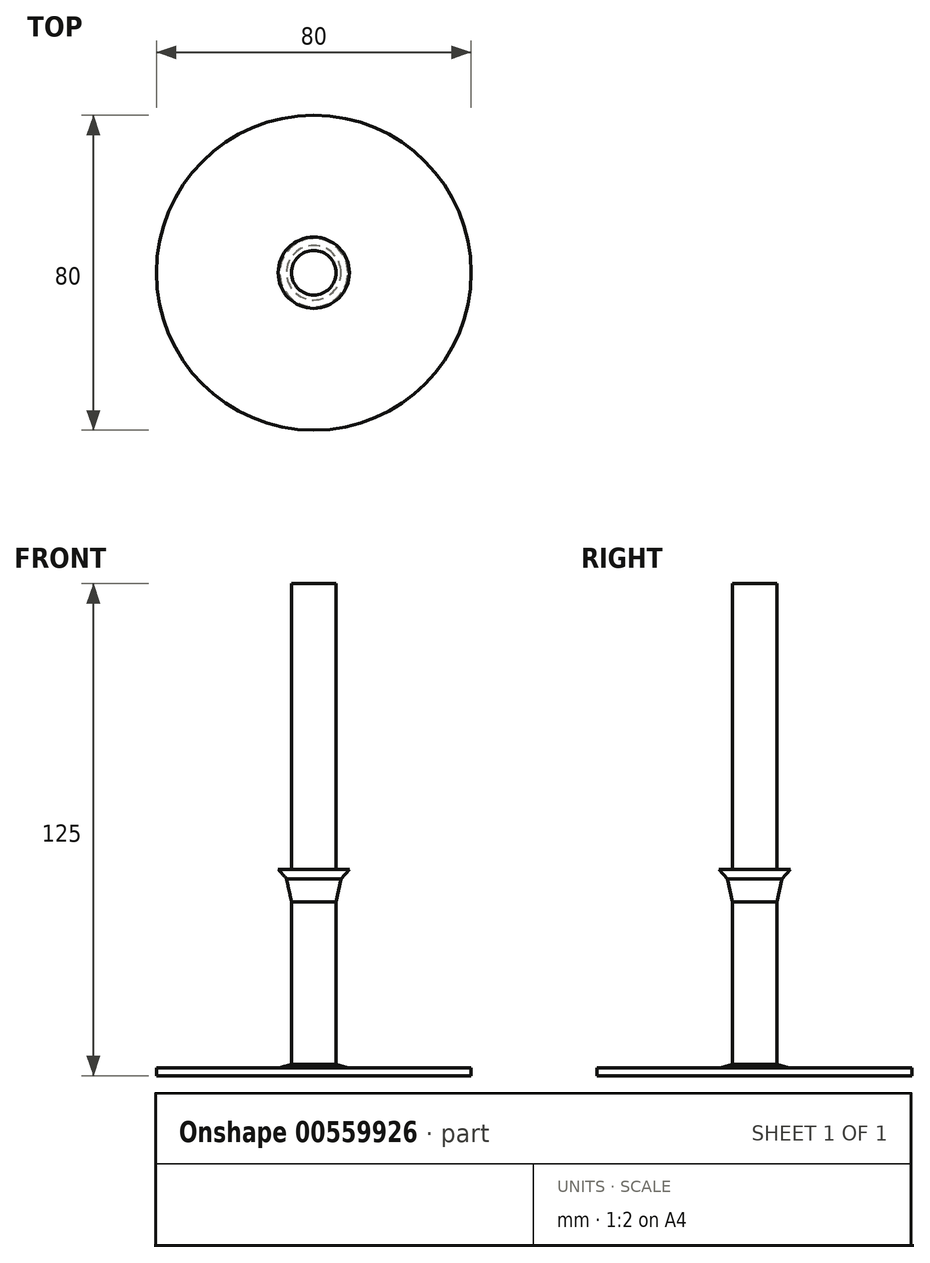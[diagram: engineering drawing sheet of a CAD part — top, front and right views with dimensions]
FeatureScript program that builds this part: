
annotation { "Feature Type Name" : "Feature", "Feature Type Description" : "" }
export const myFeature = defineFeature(function(context is Context, id is Id, definition is map)
    precondition{}
    {
        {
            var Q0;
            Q0=qCreatedBy(makeId("Front.planeOp"),FACE);
            var sketch = newSketch(context, id + "F0", { "sketchPlane" : qUnion([Q0])});
            skLineSegment(sketch, "E0", {"start": v(0, 0) * mm, "end": v(-40, 0) * mm});
            skLineSegment(sketch, "E1", {"start": v(-40, 0) * mm, "end": v(-40, 2) * mm});
            skLineSegment(sketch, "E2", {"start": v(-40, 2) * mm, "end": v(-19.77, 2) * mm});
            skLineSegment(sketch, "E3", {"start": v(-5.65, 58.65) * mm, "end": v(-5.65, 125) * mm});
            skPoint(sketch, "E4.start.orphan", {"position": v(-5.65, 63.5) * mm});
            skPoint(sketch, "E5.newPointB", {"position": v(0, 2) * mm});
            skLineSegment(sketch, "E6", {"start": v(0, 2) * mm, "end": v(0, 125) * mm});
            skLineSegment(sketch, "E7", {"start": v(0, 125) * mm, "end": v(-5.65, 125) * mm});
            skLineSegment(sketch, "E8", {"start": v(0, 0) * mm, "end": v(0, 2) * mm});
            skPoint(sketch, "E9.end.orphan", {"position": v(-5.65, 54.45) * mm});
            skPoint(sketch, "E10.orphan", {"position": v(-5.65, 2) * mm});
            skLineSegment(sketch, "E11", {"start": v(-19.77, 2) * mm, "end": v(-8.66, 2) * mm});
            skLineSegment(sketch, "E12", {"start": v(-5.65, 58.65) * mm, "end": v(-5.65, 2.87) * mm});
            skPoint(sketch, "E13.startSnap0", {"position": v(-6.22, 52.45) * mm});
            skPoint(sketch, "E13.start.orphan", {"position": v(-5.65, 52.45) * mm});
            skLineSegment(sketch, "E14", {"start": v(-5.65, 52.45) * mm, "end": v(-9.05, 52.45) * mm});
            skLineSegment(sketch, "E15", {"start": v(-9.05, 52.45) * mm, "end": v(-6.92, 50.02) * mm});
            skLineSegment(sketch, "E16", {"start": v(-6.92, 50.02) * mm, "end": v(-5.65, 44.16) * mm});
            skPoint(sketch, "E17.orphan", {"position": v(-5.65, 49.04) * mm});
            skPoint(sketch, "E18.start.orphan", {"position": v(-6.8, 55.87) * mm});
            skLineSegment(sketch, "E19", {"start": v(-8.66, 2) * mm, "end": v(-5.65, 2.87) * mm});
            skSolve(sketch);
        }
        {
            var Q0;
            Q0 = qSketchRegion(id + "F0", true);
            var Q1;
            Q1=sQuery(id+"F0.wireOp",EDGE,"E6");
            revolve(context, id + "F1", {"entities" : qUnion([Q0]), "axis" : qUnion([Q1]), "revolveType" : RevolveType.FULL});
        }
    });
